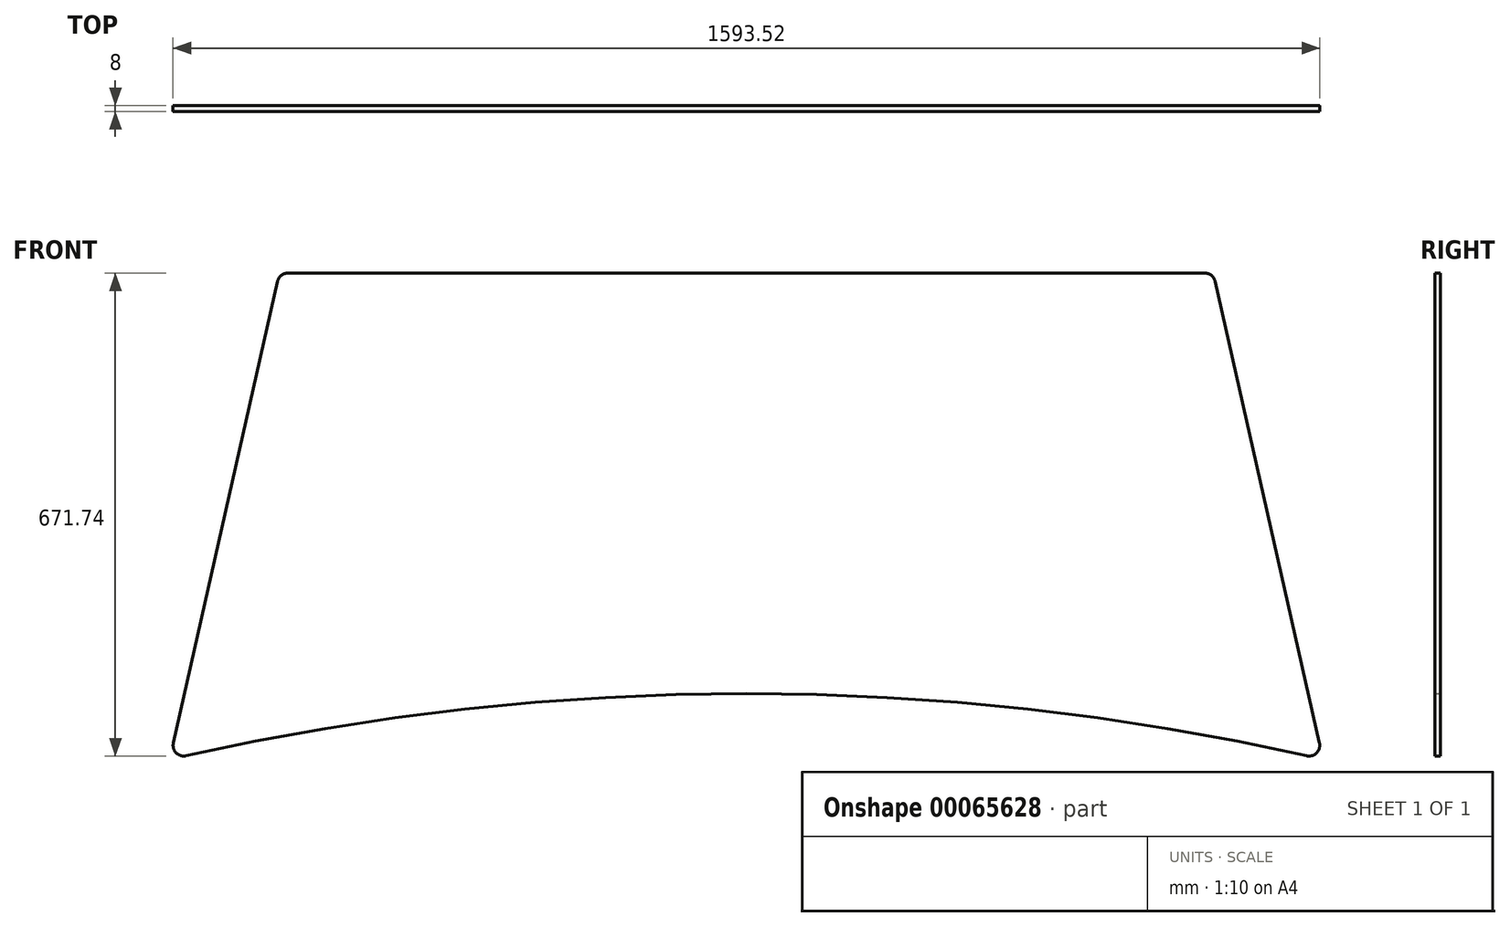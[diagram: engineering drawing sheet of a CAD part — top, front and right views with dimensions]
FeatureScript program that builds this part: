
annotation { "Feature Type Name" : "Feature", "Feature Type Description" : "" }
export const myFeature = defineFeature(function(context is Context, id is Id, definition is map)
    precondition{}
    {
        {
            var Q0;
            Q0=qCreatedBy(makeId("Front.planeOp"),FACE);
            var sketch = newSketch(context, id + "F0", { "sketchPlane" : qUnion([Q0])});
            skLineSegment(sketch, "E0", {"start": v(-795, 20.47) * mm, "end": v(-645, 685.47) * mm});
            skLineSegment(sketch, "E1", {"start": v(-645, 685.47) * mm, "end": v(0, 685.47) * mm});
            skLineSegment(sketch, "E2", {"start": v(0, 778.91) * mm, "end": v(0, 148.89) * mm, "construction": true});
            skLineSegment(sketch, "E3.MirrorCS", {"start": v(645, 685.47) * mm, "end": v(0, 685.47) * mm});
            skLineSegment(sketch, "E4.MirrorCS", {"start": v(795, 20.47) * mm, "end": v(645, 685.47) * mm});
            skArc(sketch, "E5", {"start": v(795, 20.47) * mm, "mid": v(0, 110.47) * mm, "end": v(-795, 20.47) * mm});
            skLineSegment(sketch, "E6.0", {"start": v(649, 690.47) * mm, "end": v(0, 690.47) * mm});
            skLineSegment(sketch, "E6.1", {"start": v(-649, 690.47) * mm, "end": v(0, 690.47) * mm});
            skLineSegment(sketch, "E6.2", {"start": v(801.63, 13.81) * mm, "end": v(649, 690.47) * mm});
            skArc(sketch, "E6.3", {"start": v(801.63, 13.81) * mm, "mid": v(0, 105.47) * mm, "end": v(-801.63, 13.81) * mm});
            skLineSegment(sketch, "E6.4", {"start": v(-801.63, 13.81) * mm, "end": v(-649, 690.47) * mm});
            skSolve(sketch);
        }
        {
            var Q0;
            Q0 = qSketchRegion(id + "F0", true);
            var Q1;
            Q1=makeQuery(id+"F0.imprint","IMPRINT",FACE,{"disambiguationData":[TD([[makeQuery(id+"F0.imprint","IMPRINT",EDGE,{"derivedFrom":sQuery(id+"F0.wireOp",EDGE,"E0")}),-1.0]])]});
            extrude(context, id + "F1", {"entities" : qUnion([Q0, Q1]), "flatOperationType" : FlatOperationType.REMOVE, "offsetDistance" : 25 * mm, "depth" : 8 * mm, "domain" : OperationDomain.MODEL});
        }
        {
            var Q0;
            Q0=makeQuery(id+"F1.opExtrude","SWEPT_EDGE",EDGE,{"disambiguationData":[OSD([sQuery(id+"F0.wireOp",EDGE,"E6.3"),sQuery(id+"F0.wireOp",EDGE,"E6.4")])]});
            var Q1;
            Q1=makeQuery(id+"F1.opExtrude","SWEPT_EDGE",EDGE,{"disambiguationData":[OSD([sQuery(id+"F0.wireOp",EDGE,"E6.1"),sQuery(id+"F0.wireOp",EDGE,"E6.4")])]});
            var Q2;
            Q2=makeQuery(id+"F1.opExtrude","SWEPT_EDGE",EDGE,{"disambiguationData":[OSD([sQuery(id+"F0.wireOp",EDGE,"E6.0"),sQuery(id+"F0.wireOp",EDGE,"E6.2")])]});
            var Q3;
            Q3=makeQuery(id+"F1.opExtrude","SWEPT_EDGE",EDGE,{"disambiguationData":[OSD([sQuery(id+"F0.wireOp",EDGE,"E6.2"),sQuery(id+"F0.wireOp",EDGE,"E6.3")])]});
            fillet(context, id + "F2", {"entities" : qUnion([Q0, Q1, Q2, Q3]), "radius" : 15 * mm, "tangentPropagation" : true, "allowEdgeOverflow" : false});
        }
    });
